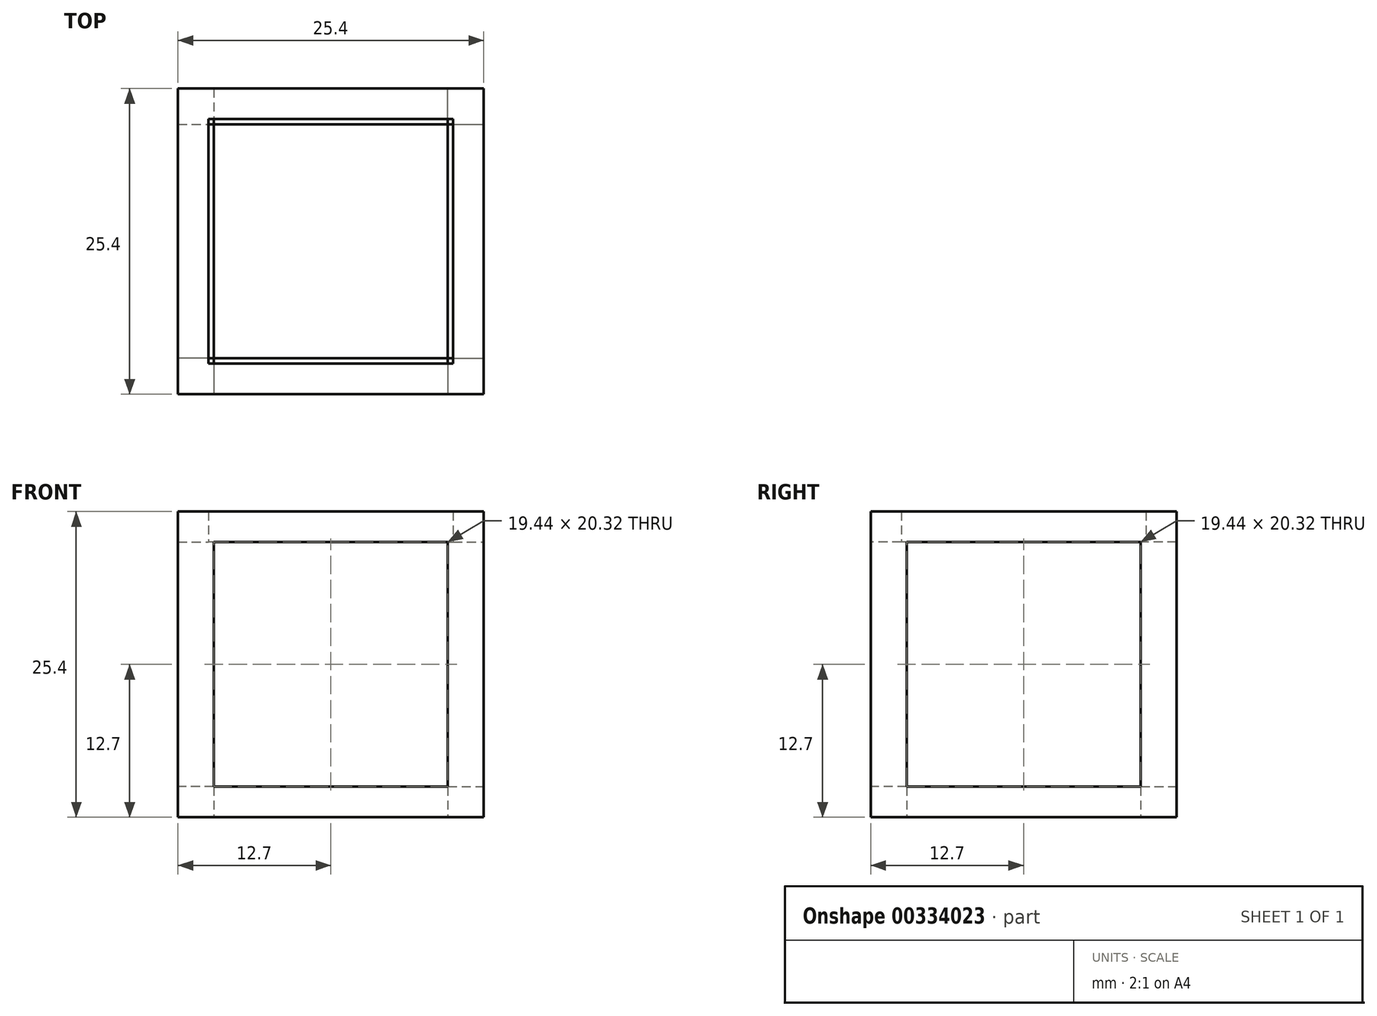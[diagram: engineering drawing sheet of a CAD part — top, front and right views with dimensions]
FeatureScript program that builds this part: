
annotation { "Feature Type Name" : "Feature", "Feature Type Description" : "" }
export const myFeature = defineFeature(function(context is Context, id is Id, definition is map)
    precondition{}
    {
        {
            var Q0;
            Q0=qCreatedBy(makeId("Top.planeOp"),FACE);
            var sketch = newSketch(context, id + "F0", { "sketchPlane" : qUnion([Q0])});
            skLineSegment(sketch, "E0", {"start": v(0, 0) * mm, "end": v(25.4, 0) * mm});
            skLineSegment(sketch, "E1", {"start": v(25.4, 0) * mm, "end": v(25.4, -25.4) * mm});
            skLineSegment(sketch, "E2", {"start": v(25.4, -25.4) * mm, "end": v(0, -25.4) * mm});
            skLineSegment(sketch, "E3", {"start": v(0, -25.4) * mm, "end": v(0, 0) * mm});
            skLineSegment(sketch, "E4.0", {"start": v(22.42, -2.98) * mm, "end": v(22.42, -22.42) * mm});
            skLineSegment(sketch, "E4.1", {"start": v(2.98, -2.98) * mm, "end": v(22.42, -2.98) * mm});
            skLineSegment(sketch, "E4.2", {"start": v(2.98, -22.42) * mm, "end": v(2.98, -2.98) * mm});
            skLineSegment(sketch, "E4.3", {"start": v(22.42, -22.42) * mm, "end": v(2.98, -22.42) * mm});
            skSolve(sketch);
        }
        {
            var Q0;
            Q0 = qSketchRegion(id + "F0", true);
            extrude(context, id + "F1", {"entities" : qUnion([Q0]), "depth" : 2.54 * mm});
        }
        {
            var Q0;
            Q0=makeQuery(id+"F1.opExtrude","CAP_FACE",FACE,{"disambiguationData":[OSD([sQuery(id+"F0.wireOp",EDGE,"E0"),sQuery(id+"F0.wireOp",EDGE,"E1"),sQuery(id+"F0.wireOp",EDGE,"E2"),sQuery(id+"F0.wireOp",EDGE,"E3"),sQuery(id+"F0.wireOp",EDGE,"E4.0"),sQuery(id+"F0.wireOp",EDGE,"E4.1"),sQuery(id+"F0.wireOp",EDGE,"E4.2"),sQuery(id+"F0.wireOp",EDGE,"E4.3")])],"isStart":false});
            var sketch = newSketch(context, id + "F2", { "sketchPlane" : qUnion([Q0])});
            skLineSegment(sketch, "E5.bottom", {"start": v(0, 0) * mm, "end": v(2.98, 0) * mm});
            skLineSegment(sketch, "E5.top", {"start": v(0, -2.98) * mm, "end": v(2.98, -2.98) * mm});
            skLineSegment(sketch, "E5.left", {"start": v(0, 0) * mm, "end": v(0, -2.98) * mm});
            skLineSegment(sketch, "E5.right", {"start": v(2.98, 0) * mm, "end": v(2.98, -2.98) * mm});
            skLineSegment(sketch, "E6.bottom", {"start": v(22.42, -2.98) * mm, "end": v(25.4, -2.98) * mm});
            skLineSegment(sketch, "E6.top", {"start": v(22.42, 0) * mm, "end": v(25.4, 0) * mm});
            skLineSegment(sketch, "E6.left", {"start": v(22.42, -2.98) * mm, "end": v(22.42, 0) * mm});
            skLineSegment(sketch, "E6.right", {"start": v(25.4, -2.98) * mm, "end": v(25.4, 0) * mm});
            skLineSegment(sketch, "E7.bottom", {"start": v(22.42, -22.42) * mm, "end": v(25.4, -22.42) * mm});
            skLineSegment(sketch, "E7.top", {"start": v(22.42, -25.4) * mm, "end": v(25.4, -25.4) * mm});
            skLineSegment(sketch, "E7.left", {"start": v(22.42, -22.42) * mm, "end": v(22.42, -25.4) * mm});
            skLineSegment(sketch, "E7.right", {"start": v(25.4, -22.42) * mm, "end": v(25.4, -25.4) * mm});
            skLineSegment(sketch, "E8.bottom", {"start": v(2.98, -22.42) * mm, "end": v(0, -22.42) * mm});
            skLineSegment(sketch, "E8.top", {"start": v(2.98, -25.4) * mm, "end": v(0, -25.4) * mm});
            skLineSegment(sketch, "E8.left", {"start": v(2.98, -22.42) * mm, "end": v(2.98, -25.4) * mm});
            skLineSegment(sketch, "E8.right", {"start": v(0, -22.42) * mm, "end": v(0, -25.4) * mm});
            skSolve(sketch);
        }
        {
            var Q0;
            Q0 = qSketchRegion(id + "F2", true);
            extrude(context, id + "F3", {"entities" : qUnion([Q0]), "operationType" : NewBodyOperationType.ADD, "depth" : 20.32 * mm});
        }
        {
            var Q0;
            Q0=qCreatedBy(makeId("Top.planeOp"),FACE);
            cPlane(context, id + "F4", {"entities" : qUnion([Q0]), "cplaneType" : CPlaneType.OFFSET, "offset" : 22.86 * mm, "width" : 152.4 * mm, "height" : 152.4 * mm});
        }
        {
            var Q0;
            Q0=qCreatedBy(id+"F4.planeOp",FACE);
            var sketch = newSketch(context, id + "F5", { "sketchPlane" : qUnion([Q0])});
            skLineSegment(sketch, "E9", {"start": v(0, 0) * mm, "end": v(25.4, 0) * mm});
            skLineSegment(sketch, "E10", {"start": v(25.4, -25.4) * mm, "end": v(25.4, 0) * mm});
            skLineSegment(sketch, "E11", {"start": v(0, 0) * mm, "end": v(0, -25.4) * mm});
            skLineSegment(sketch, "E12", {"start": v(0, -25.4) * mm, "end": v(25.4, -25.4) * mm});
            skLineSegment(sketch, "E13.0", {"start": v(2.54, -2.54) * mm, "end": v(2.54, -22.86) * mm});
            skLineSegment(sketch, "E13.1", {"start": v(2.54, -2.54) * mm, "end": v(22.86, -2.54) * mm});
            skLineSegment(sketch, "E13.2", {"start": v(22.86, -22.86) * mm, "end": v(22.86, -2.54) * mm});
            skLineSegment(sketch, "E13.3", {"start": v(2.54, -22.86) * mm, "end": v(22.86, -22.86) * mm});
            skLineSegment(sketch, "E14.bottom", {"start": v(22.86, -2.54) * mm, "end": v(25.4, -2.54) * mm});
            skLineSegment(sketch, "E14.top", {"start": v(22.86, 0) * mm, "end": v(25.4, 0) * mm});
            skLineSegment(sketch, "E14.left", {"start": v(22.86, -2.54) * mm, "end": v(22.86, 0) * mm});
            skLineSegment(sketch, "E14.right", {"start": v(25.4, -2.54) * mm, "end": v(25.4, 0) * mm});
            skLineSegment(sketch, "E15.bottom", {"start": v(0, 0) * mm, "end": v(2.54, 0) * mm});
            skLineSegment(sketch, "E15.top", {"start": v(0, -2.54) * mm, "end": v(2.54, -2.54) * mm});
            skLineSegment(sketch, "E15.left", {"start": v(0, 0) * mm, "end": v(0, -2.54) * mm});
            skLineSegment(sketch, "E15.right", {"start": v(2.54, 0) * mm, "end": v(2.54, -2.54) * mm});
            skLineSegment(sketch, "E16.bottom", {"start": v(0, -25.4) * mm, "end": v(2.54, -25.4) * mm});
            skLineSegment(sketch, "E16.top", {"start": v(0, -22.86) * mm, "end": v(2.54, -22.86) * mm});
            skLineSegment(sketch, "E16.left", {"start": v(0, -25.4) * mm, "end": v(0, -22.86) * mm});
            skLineSegment(sketch, "E16.right", {"start": v(2.54, -25.4) * mm, "end": v(2.54, -22.86) * mm});
            skLineSegment(sketch, "E17.bottom", {"start": v(25.4, -25.4) * mm, "end": v(22.86, -25.4) * mm});
            skLineSegment(sketch, "E17.top", {"start": v(25.4, -22.86) * mm, "end": v(22.86, -22.86) * mm});
            skLineSegment(sketch, "E17.left", {"start": v(25.4, -25.4) * mm, "end": v(25.4, -22.86) * mm});
            skLineSegment(sketch, "E17.right", {"start": v(22.86, -25.4) * mm, "end": v(22.86, -22.86) * mm});
            skSolve(sketch);
        }
        {
            var Q0;
            Q0 = qSketchRegion(id + "F5", true);
            extrude(context, id + "F6", {"entities" : qUnion([Q0]), "operationType" : NewBodyOperationType.ADD, "depth" : 2.54 * mm});
        }
    });
